# Revit family: Urinal-Willoughby-1800-UW-FA-RS
name_source: partatom
category: Plumbing Fixtures
revit_build: Autodesk Revit 2014 (Build: 20130308_1515(x64)
units: mm (PartAtom-declared; Revit-internal decimal feet)

## types (5) — shared parameters
CW Connection = Yes
Default Elevation = 0' - 0"
HW Connection = No
Manufacturer = Willoughby Industries
Revision = A
URL = willoughby-ind.com
Vent Connection = No
Waste Connection = Yes
Waste DIA = 2"

## per-type parameters (varying)
| type | 36" | 48" | 60" | 72" | 96" | CW inlet Diameter | Description | Fixture Body | Half Width | Model | Trough Width | Width |
| 1848 | No | Yes | No | No | No | 1" | 48" Trough Urinal | Stainless Steel AISI 304-Willoughby(2) | 2' - 0" | UW-1836-FA-RS | 3' - 8 1/2" | 4' - 0" |
| 1836 | Yes | No | No | No | No | 1" | 36" Trough Urinal | Stainless Steel AISI 304-Willoughby(3) | 1' - 6" | UW-1836-FA-RS | 2' - 8 1/2" | 3' - 0" |
| 1860 | No | No | Yes | No | No | 1" | 60" Trough Urinal | Stainless Steel AISI 304-Willoughby(1) | 2' - 6" | UW-1836-FA-RS | 4' - 8 1/2" | 5' - 0" |
| 1872 | No | No | No | Yes | No | 2" | 72" Trough Urinal | Stainless Steel AISI 304-Willoughby | 3' - 0" | UW-1836-FA-RS | 5' - 8 1/2" | 6' - 0" |
| 1896 | No | No | No | No | Yes | 2" | 96" Trough Urinal | Stainless Steel AISI 304-Willoughby(4) | 4' - 0" | UW-1836-FA-TS-RS | 7' - 8 1/2" | 8' - 0" |

## geometry (parser evidence)
native form markers: Sweep x1
no freeform markers — native parametric forms only
